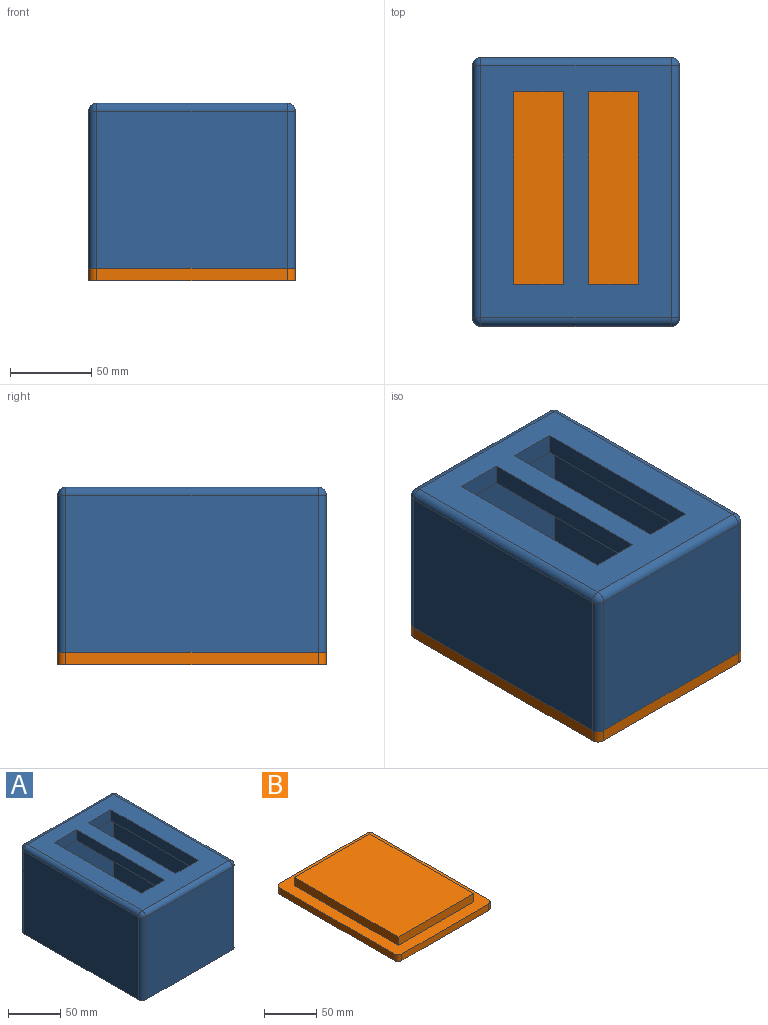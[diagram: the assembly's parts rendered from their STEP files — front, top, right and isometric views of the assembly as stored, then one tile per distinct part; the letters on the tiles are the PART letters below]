
ASSEMBLY  parts=2 mates=1
PART A: 31 faces, bbox 127x165.1x101.6 mm
  f0: plane 154.94x116.84mm, normal (0,0,1), area 10853.2mm2, adj f12,f17,f18,f22,f23,f24,f25,f26
  f1: plane 139.7x101.6mm, normal (0,0,-1), area 6943.6mm2, adj f7,f8,f9,f10,f23,f24,f25,f26
  f2: plane 165.1x127mm, normal (0,0,-1), area 6752mm2, adj f3,f4,f5,f6,f7,f8,f9,f10
  f3: plane 154.94x96.52mm, normal (-1,0,0), area 14954.8mm2, adj f2,f11,f12,f13
  f4: plane 154.94x96.52mm, normal (1,0,0), area 14954.8mm2, adj f2,f16,f19,f22
  f5: plane 116.84x96.52mm, normal (0,-1,0), area 11277.4mm2, adj f2,f11,f16,f17
  f6: plane 116.84x96.52mm, normal (0,1,0), area 11277.4mm2, adj f2,f13,f18,f19
  f7: plane 139.7x88.9mm, normal (1,0,0), area 12419.3mm2, adj f1,f2,f9,f10
  f8: plane 139.7x88.9mm, normal (-1,0,0), area 12419.3mm2, adj f1,f2,f9,f10
  f9: plane 101.6x88.9mm, normal (0,1,0), area 9032.2mm2, adj f1,f2,f7,f8
  f10: plane 101.6x88.9mm, normal (0,-1,0), area 9032.2mm2, adj f1,f2,f7,f8
  f11: cylinder r=5.08mm len=96.52mm, axis (0,0,1), area 770.2mm2, adj f2,f3,f5,f14
  f12: cylinder r=5.08mm len=154.94mm, axis (0,1,0), area 1236.4mm2, adj f0,f3,f14,f15
  f13: cylinder r=5.08mm len=96.52mm, axis (0,0,-1), area 770.2mm2, adj f2,f3,f6,f15
  f14: sphere r=5.08mm, area 40.5mm2, adj f11,f12,f17
  f15: sphere r=5.08mm, area 40.5mm2, adj f12,f13,f18
  f16: cylinder r=5.08mm len=96.52mm, axis (0,0,-1), area 770.2mm2, adj f2,f4,f5,f20
  f17: cylinder r=5.08mm len=116.84mm, axis (1,0,0), area 932.3mm2, adj f0,f5,f14,f20
  f18: cylinder r=5.08mm len=116.84mm, axis (-1,0,0), area 932.3mm2, adj f0,f6,f15,f21
  f19: cylinder r=5.08mm len=96.52mm, axis (0,0,1), area 770.2mm2, adj f2,f4,f6,f21
  f20: sphere r=5.08mm, area 40.5mm2, adj f16,f17,f22
  f21: sphere r=5.08mm, area 40.5mm2, adj f18,f19,f22
  f22: cylinder r=5.08mm len=154.94mm, axis (0,-1,0), area 1236.4mm2, adj f0,f4,f20,f21
  f23: plane 118.34x12.7mm, normal (-1,0,0), area 1502.9mm2, adj f0,f1,f24,f26
  f24: plane 30.63x12.7mm, normal (0,-1,0), area 389mm2, adj f0,f1,f23,f25
  f25: plane 118.34x12.7mm, normal (1,0,0), area 1502.9mm2, adj f0,f1,f24,f26
  f26: plane 30.63x12.7mm, normal (0,1,0), area 389mm2, adj f0,f1,f23,f25
  f27: plane 30.63x12.7mm, normal (0,-1,0), area 389mm2, adj f0,f1,f28,f30
  f28: plane 118.34x12.7mm, normal (1,0,0), area 1502.9mm2, adj f0,f1,f27,f29
  f29: plane 30.63x12.7mm, normal (0,1,0), area 389mm2, adj f0,f1,f28,f30
  f30: plane 118.34x12.7mm, normal (-1,0,0), area 1502.9mm2, adj f0,f1,f27,f29
PART B: 15 faces, bbox 127x165.1x17.3 mm
  f0: plane 165.1x127mm, normal (0,0,1), area 6752mm2, adj f1,f2,f3,f4,f6,f7,f8,f9
  f1: plane 154.94x7.62mm, normal (-1,0,0), area 1180.6mm2, adj f0,f5,f11,f14
  f2: plane 116.84x7.62mm, normal (0,-1,0), area 890.3mm2, adj f0,f5,f11,f12
  f3: plane 154.94x7.62mm, normal (1,0,0), area 1180.6mm2, adj f0,f5,f12,f13
  f4: plane 116.84x7.62mm, normal (0,1,0), area 890.3mm2, adj f0,f5,f13,f14
  f5: plane 165.1x127mm, normal (0,0,-1), area 20945.5mm2, adj f1,f2,f3,f4,f11,f12,f13,f14
  f6: plane 139.7x9.65mm, normal (-1,0,0), area 1348.4mm2, adj f0,f7,f9,f10
  f7: plane 101.6x9.65mm, normal (0,-1,0), area 980.6mm2, adj f0,f6,f8,f10
  f8: plane 139.7x9.65mm, normal (1,0,0), area 1348.4mm2, adj f0,f7,f9,f10
  f9: plane 101.6x9.65mm, normal (0,1,0), area 980.6mm2, adj f0,f6,f8,f10
  f10: plane 139.7x101.6mm, normal (0,0,1), area 14193.5mm2, adj f6,f7,f8,f9
  f11: cylinder r=5.08mm len=7.62mm, axis (0,0,1), area 60.8mm2, adj f0,f1,f2,f5
  f12: cylinder r=5.08mm len=7.62mm, axis (0,0,-1), area 60.8mm2, adj f0,f2,f3,f5
  f13: cylinder r=5.08mm len=7.62mm, axis (0,0,1), area 60.8mm2, adj f0,f3,f4,f5
  f14: cylinder r=5.08mm len=7.62mm, axis (0,0,-1), area 60.8mm2, adj f0,f1,f4,f5
PLACE A rot(axis=(1,0,0),0deg) t=(0,82.55,58.42)mm
PLACE B at identity
MATE fastened A.f2 <-> B.f0  axis (0,0,1) through (50.8,-69.85,7.62)mm
